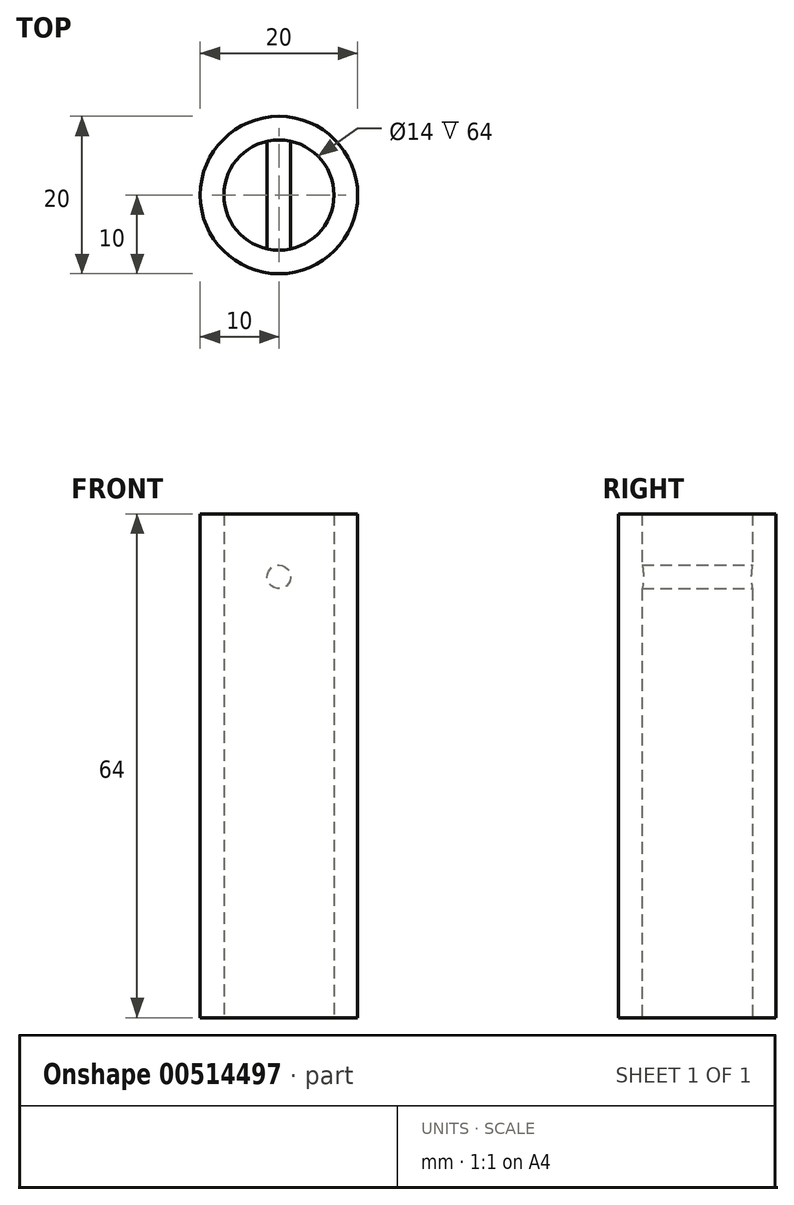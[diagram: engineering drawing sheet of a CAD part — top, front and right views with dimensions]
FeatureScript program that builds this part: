
annotation { "Feature Type Name" : "Feature", "Feature Type Description" : "" }
export const myFeature = defineFeature(function(context is Context, id is Id, definition is map)
    precondition{}
    {
        {
            var Q0;
            Q0=qCreatedBy(makeId("Top.planeOp"),FACE);
            var sketch = newSketch(context, id + "F0", { "sketchPlane" : qUnion([Q0])});
            skCircle(sketch, "E0", {"center": v(0, 0) * mm, "radius": 10 * mm});
            skCircle(sketch, "E1", {"center": v(0, 0) * mm, "radius": 7 * mm});
            skSolve(sketch);
        }
        {
            var Q0;
            Q0=makeQuery(id+"F0.imprint","IMPRINT",FACE,{"disambiguationData":[TD([[makeQuery(id+"F0.imprint","IMPRINT",EDGE,{"derivedFrom":sQuery(id+"F0.wireOp",EDGE,"E0")}),1.0]])]});
            extrude(context, id + "F1", {"entities" : qUnion([Q0]), "depth" : 64 * mm, "offsetDistance" : 25 * mm});
        }
        {
            var Q0;
            Q0=qCreatedBy(makeId("Front.planeOp"),FACE);
            var sketch = newSketch(context, id + "F2", { "sketchPlane" : qUnion([Q0])});
            skCircle(sketch, "E2", {"center": v(0, 56) * mm, "radius": 1.5 * mm});
            skSolve(sketch);
        }
        {
            var Q0;
            Q0=makeQuery(id+"F2.imprint","IMPRINT",FACE,{"disambiguationData":[TD([[makeQuery(id+"F2.imprint","IMPRINT",EDGE,{"derivedFrom":sQuery(id+"F2.wireOp",EDGE,"E2")}),1.0]])]});
            extrude(context, id + "F3", {"entities" : qUnion([Q0]), "operationType" : NewBodyOperationType.ADD, "endBound" : BoundingType.SYMMETRIC, "depth" : 18 * mm, "offsetDistance" : 25 * mm});
        }
    });
